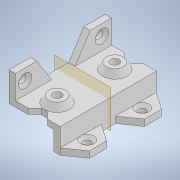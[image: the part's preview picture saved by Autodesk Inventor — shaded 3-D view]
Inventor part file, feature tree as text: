
AUTODESK INVENTOR PART (.ipt)
format: ipt  version: 2022 (Build 260153000, 153)  size: 241,152 bytes
history: native  units: mm
features: sketch x7, extrude x6, projected_geometry x5, hole x2, draft x2, plane x1
ambient origin geometry x8: Origin, YZ Plane, XZ Plane, XY Plane, X Axis, Y Axis, Z Axis, Center Point
bodies: Solid1 (feature_tree)
feature tree (23):
  extrude  "Extrusion1"  Depth=21.0mm
  extrude  "Extrusion2"  Depth=3.0mm
  plane  "Work Plane1"
  extrude  "Extrusion3"  Depth=11.0mm
  hole  "Hole1"  [1 undecoded]
  extrude  "Extrusion4"  TaperAngle=0.0deg  [1 undecoded]
  hole  "Hole2"  [1 undecoded]
  sketch  "Sketch7"  dims[d16=3.0mm d17=3.0mm d18=3.0mm d19=0.0mm d20=0.0mm d21=4.5mm d22=4.5mm d23=3.6mm d24=6.0mm d25=6.3mm d26=2.0mm d27=90.0deg d28=8.0mm d29=20.594885mm d30=8.0mm d31=8.0mm d32=8.0mm d33=8.0mm d36=3.0mm d37=0.0mm d38=11.0mm d39=3.6mm d40=6.0mm d41=6.3mm d42=2.0mm d43=90.0deg d44=8.0mm d45=20.594885mm d46=5.15mm d48=4.0mm d49=13.5mm d50=13.5mm d51=8.0mm d52=3.0mm d53=0.0mm d54=1.0mm d55=0.0mm d59=30.0deg d60=30.0deg d61=27.0mm d62=3.0mm d66=5.598261mm d67=5.598261mm]
  extrude  "Extrusion5"  Depth=3.0mm
  extrude  "Extrusion6"  Depth=3.0mm
  draft  "FaceDraft1"
  draft  "FaceDraft2"
  sketch  "Sketch1"  dims[d0=2.65mm d1=21.0mm]
  sketch  "Sketch2"  dims[d2=9.0mm d3=3.0mm]
  projected_geometry  "Projected Loop1"
  sketch  "Sketch3"  dims[d4=3.0mm d5=11.0mm]
  projected_geometry  "Projected Loop2"
  sketch  "Sketch4"  dims[d6=45.0mm d7=0.0mm d10=10.0mm]
  sketch  "Sketch5"  dims[d11=10.0mm d12=0.0mm d13=0.0mm]
  projected_geometry  "Projected Loop3"
  sketch  "Sketch6"  dims[d14=45.0deg d15=45.0deg]
  projected_geometry  "Projected Loop4"
  projected_geometry  "Projected Loop5"
note: 3 required parameter values undecoded (feature->parameter linkage not recoverable at this tier; creation-order binding heuristic only, values carry confidence <= 0.55)
